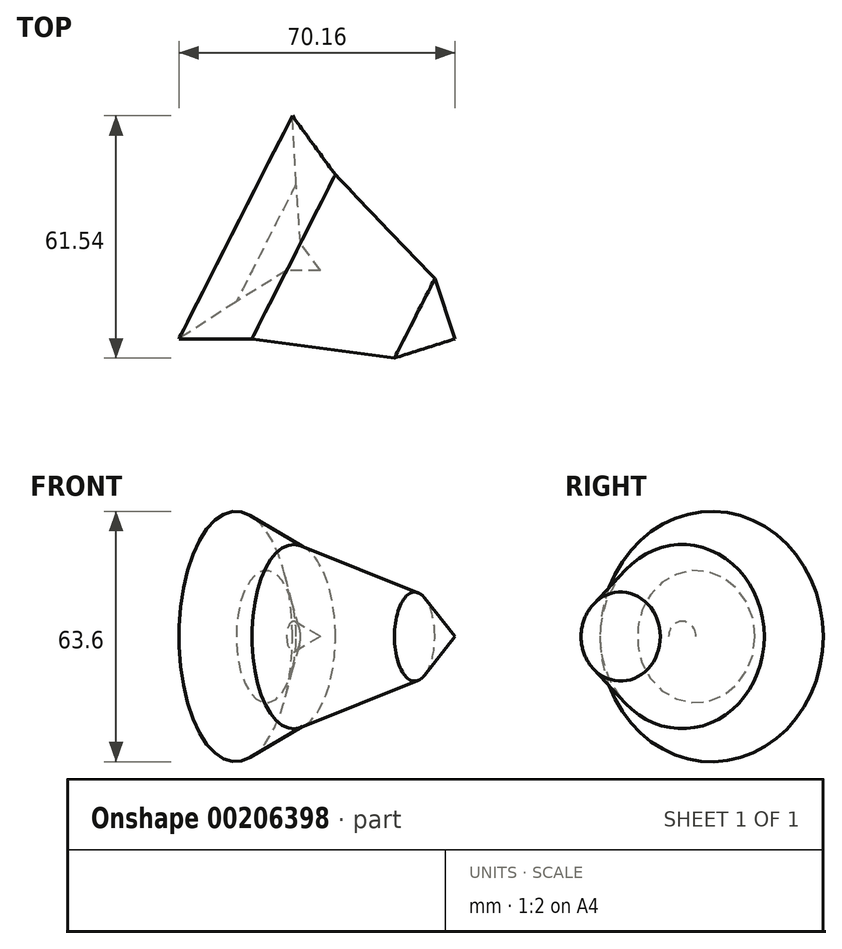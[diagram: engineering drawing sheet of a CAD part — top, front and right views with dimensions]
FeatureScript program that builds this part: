
annotation { "Feature Type Name" : "Feature", "Feature Type Description" : "" }
export const myFeature = defineFeature(function(context is Context, id is Id, definition is map)
    precondition{}
    {
        {
            var Q0;
            Q0=qCreatedBy(makeId("Top.planeOp"),FACE);
            var sketch = newSketch(context, id + "F0", { "sketchPlane" : qUnion([Q0])});
            skLineSegment(sketch, "E0", {"start": v(-47.06, -31.8) * mm, "end": v(-28.52, -31.8) * mm});
            skLineSegment(sketch, "E1", {"start": v(-28.52, -31.8) * mm, "end": v(7.7, -36.65) * mm});
            skLineSegment(sketch, "E2", {"start": v(7.7, -36.65) * mm, "end": v(23.1, -31.8) * mm});
            skLineSegment(sketch, "E3", {"start": v(23.1, -31.8) * mm, "end": v(-11.12, -14.4) * mm});
            skLineSegment(sketch, "E4", {"start": v(-11.12, -14.4) * mm, "end": v(-19.68, -14.4) * mm});
            skLineSegment(sketch, "E5", {"start": v(-19.68, -14.4) * mm, "end": v(-32.52, -22.4) * mm});
            skLineSegment(sketch, "E6", {"start": v(-32.52, -22.4) * mm, "end": v(-47.06, -31.8) * mm});
            skSolve(sketch);
        }
        {
            var Q0;
            Q0=makeQuery(id+"F0.imprint","IMPRINT",FACE,{"disambiguationData":[TD([[makeQuery(id+"F0.imprint","IMPRINT",EDGE,{"derivedFrom":sQuery(id+"F0.wireOp",EDGE,"E0")}),1.0]])]});
            var Q1;
            Q1=sQuery(id+"F0.wireOp",EDGE,"E3");
            revolve(context, id + "F1", {"entities" : qUnion([Q0]), "axis" : qUnion([Q1]), "revolveType" : RevolveType.FULL});
        }
    });
